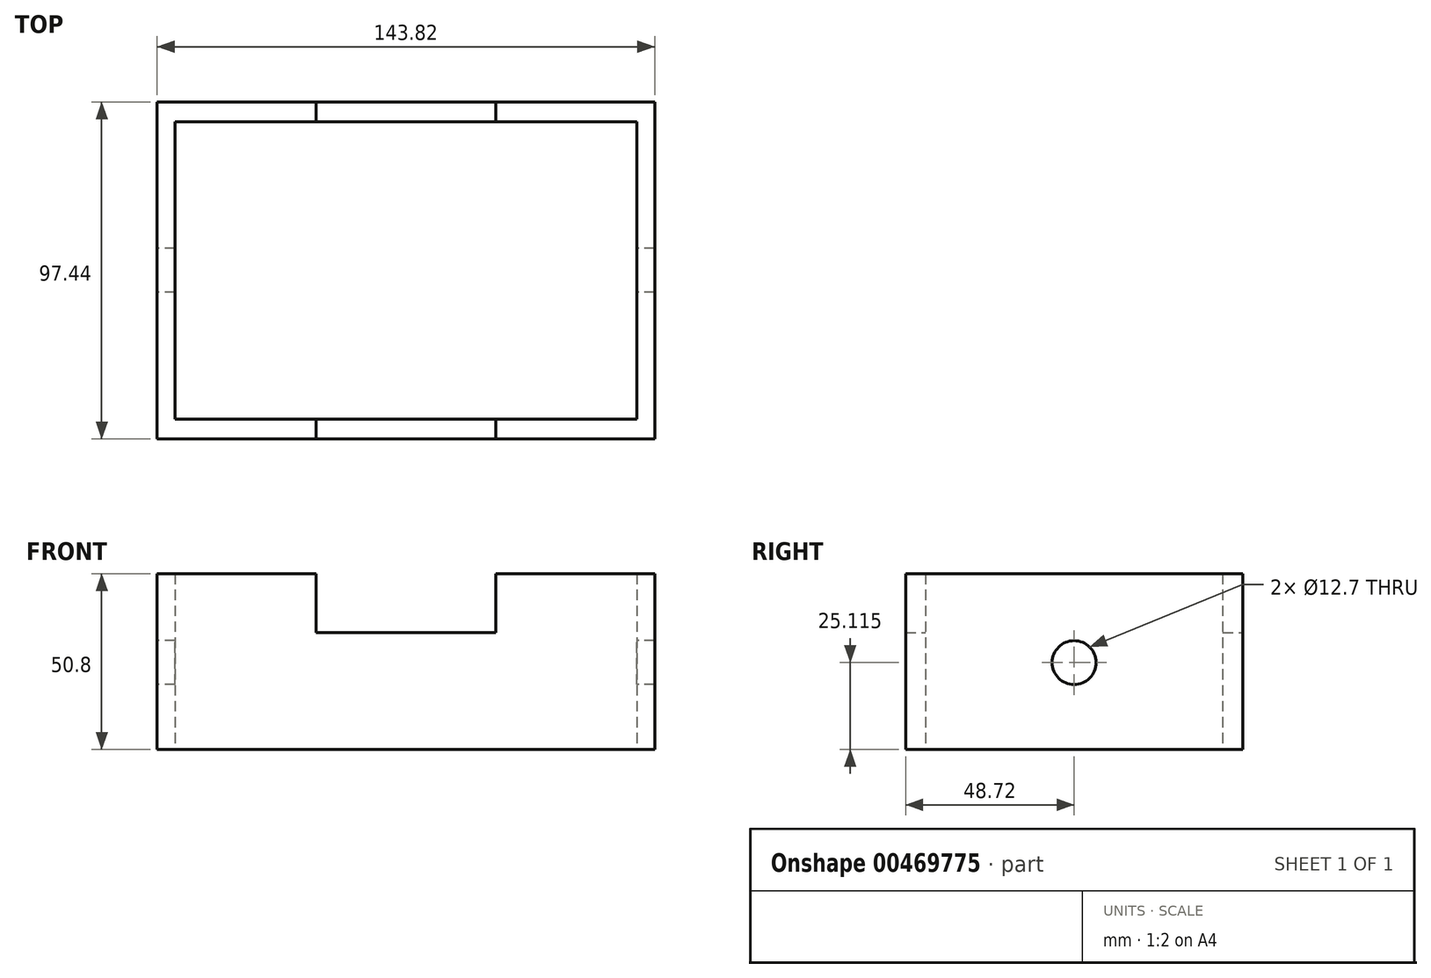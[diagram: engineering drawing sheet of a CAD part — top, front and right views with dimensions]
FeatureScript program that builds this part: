
annotation { "Feature Type Name" : "Feature", "Feature Type Description" : "" }
export const myFeature = defineFeature(function(context is Context, id is Id, definition is map)
    precondition{}
    {
        {
            var Q0;
            Q0=qCreatedBy(makeId("Top.planeOp"),FACE);
            var sketch = newSketch(context, id + "F0", { "sketchPlane" : qUnion([Q0])});
            skLineSegment(sketch, "E0.bottom", {"start": v(-71.91, 48.72) * mm, "end": v(71.91, 48.72) * mm});
            skLineSegment(sketch, "E0.top", {"start": v(-71.91, -48.72) * mm, "end": v(71.91, -48.72) * mm});
            skLineSegment(sketch, "E0.left", {"start": v(-71.91, 48.72) * mm, "end": v(-71.91, -48.72) * mm});
            skLineSegment(sketch, "E0.right", {"start": v(71.91, 48.72) * mm, "end": v(71.91, -48.72) * mm});
            skPoint(sketch, "E0.middle", {"position": v(0, 0) * mm});
            skLineSegment(sketch, "E1.bottom", {"start": v(-66.7, 42.96) * mm, "end": v(66.7, 42.96) * mm});
            skLineSegment(sketch, "E1.top", {"start": v(-66.7, -42.96) * mm, "end": v(66.7, -42.96) * mm});
            skLineSegment(sketch, "E1.left", {"start": v(-66.7, 42.96) * mm, "end": v(-66.7, -42.96) * mm});
            skLineSegment(sketch, "E1.right", {"start": v(66.7, 42.96) * mm, "end": v(66.7, -42.96) * mm});
            skSolve(sketch);
        }
        {
            var Q0;
            Q0=makeQuery(id+"F0.imprint","IMPRINT",FACE,{"disambiguationData":[TD([[makeQuery(id+"F0.imprint","IMPRINT",EDGE,{"derivedFrom":sQuery(id+"F0.wireOp",EDGE,"E0.bottom")}),-1.0]])]});
            extrude(context, id + "F1", {"entities" : qUnion([Q0]), "depth" : 50.8 * mm});
        }
        {
            var Q0;
            Q0=makeQuery(id+"F1.opExtrude","SWEPT_FACE",FACE,{"disambiguationData":[OSD([sQuery(id+"F0.wireOp",EDGE,"E0.bottom")])]});
            var sketch = newSketch(context, id + "F2", { "sketchPlane" : qUnion([Q0])});
            skLineSegment(sketch, "E2.bottom", {"start": v(-25.97, 50.8) * mm, "end": v(25.97, 50.8) * mm});
            skLineSegment(sketch, "E2.top", {"start": v(-25.97, 33.77) * mm, "end": v(25.97, 33.77) * mm});
            skLineSegment(sketch, "E2.left", {"start": v(-25.97, 50.8) * mm, "end": v(-25.97, 33.77) * mm});
            skLineSegment(sketch, "E2.right", {"start": v(25.97, 50.8) * mm, "end": v(25.97, 33.77) * mm});
            skPoint(sketch, "E2.middle", {"position": v(0, 42.29) * mm});
            skSolve(sketch);
        }
        {
            var Q0;
            Q0=makeQuery(id+"F2.imprint","IMPRINT",FACE,{"disambiguationData":[TD([[makeQuery(id+"F2.imprint","IMPRINT",EDGE,{"derivedFrom":sQuery(id+"F2.wireOp",EDGE,"E2.bottom")}),1.0]])]});
            extrude(context, id + "F3", {"entities" : qUnion([Q0]), "operationType" : NewBodyOperationType.REMOVE, "endBound" : BoundingType.THROUGH_ALL, "oppositeDirection" : true, "depth" : 25.4 * mm});
        }
        {
            var Q0;
            Q0=makeQuery(id+"F1.opExtrude","SWEPT_FACE",FACE,{"disambiguationData":[OSD([sQuery(id+"F0.wireOp",EDGE,"E0.left")])]});
            var sketch = newSketch(context, id + "F4", { "sketchPlane" : qUnion([Q0])});
            skPoint(sketch, "E3", {"position": v(0, 25.11) * mm});
            skSolve(sketch);
        }
        {
            var Q0;
            Q0=sQuery(id+"F4.wireOp",VERTEX,"E3");
            var Q1;
            Q1=makeQuery(id+"F1.opExtrude","SWEPT_BODY",BODY,{"disambiguationData":[OSD([sQuery(id+"F0.wireOp",EDGE,"E0.bottom"),sQuery(id+"F0.wireOp",EDGE,"E0.top"),sQuery(id+"F0.wireOp",EDGE,"E0.left"),sQuery(id+"F0.wireOp",EDGE,"E0.right"),sQuery(id+"F0.wireOp",EDGE,"E1.bottom"),sQuery(id+"F0.wireOp",EDGE,"E1.top"),sQuery(id+"F0.wireOp",EDGE,"E1.left"),sQuery(id+"F0.wireOp",EDGE,"E1.right")])]});
            hole(context, id + "F5", {"style" : HoleStyle.SIMPLE, "endStyle" : HoleEndStyle.THROUGH, "holeDiameter" : 12.7 * mm, "isTappedThrough" : true, "tappedDepth" : 12.7 * mm, "tapClearance" : 3, "locations" : qUnion([Q0]), "scope" : qUnion([Q1])});
        }
    });
